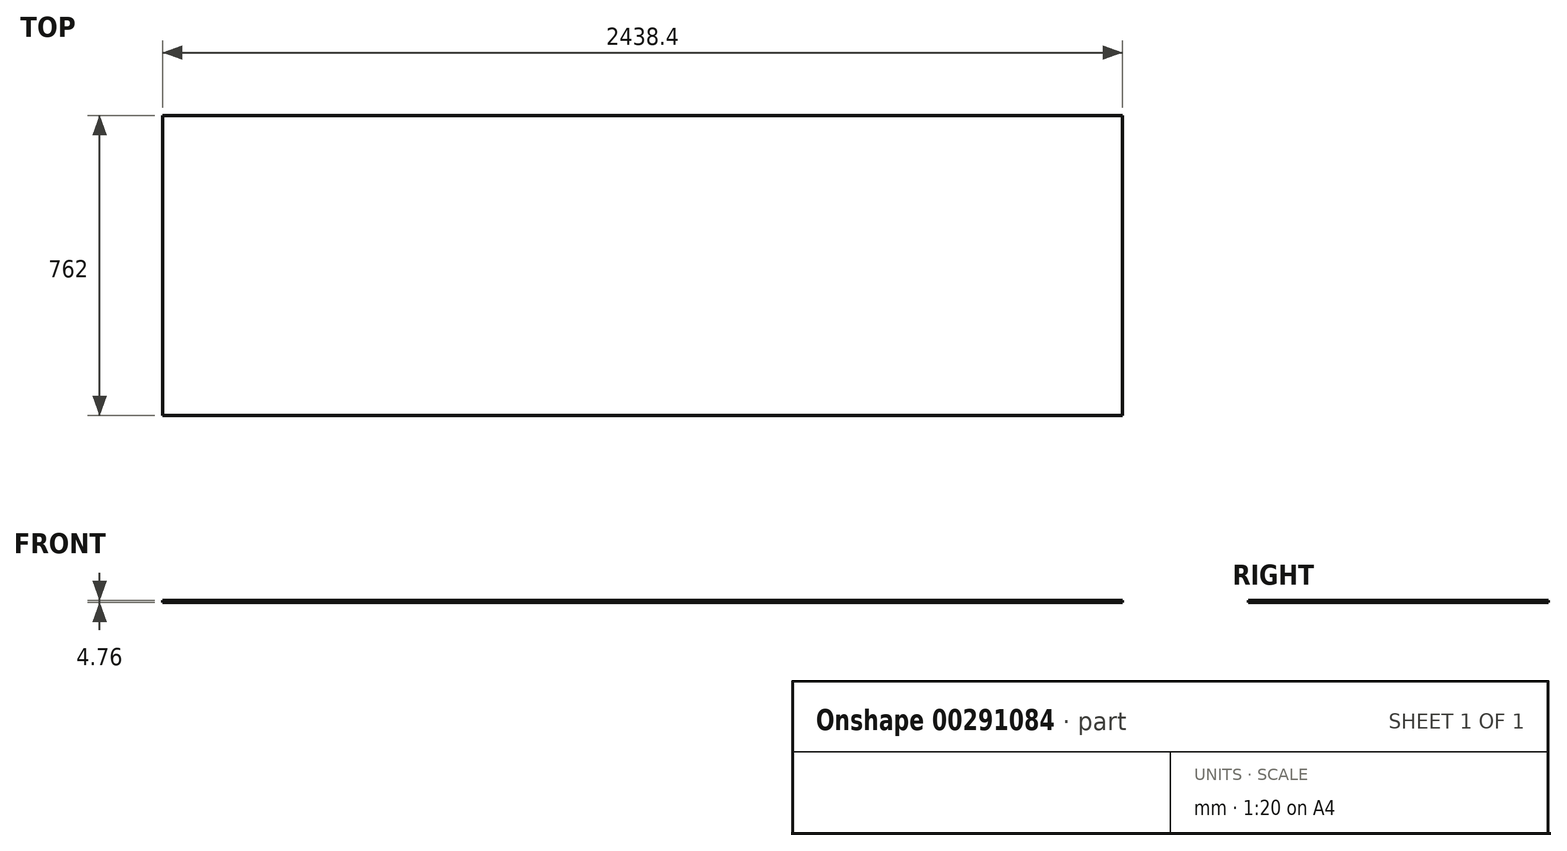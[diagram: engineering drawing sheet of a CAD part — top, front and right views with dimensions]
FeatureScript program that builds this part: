
annotation { "Feature Type Name" : "Feature", "Feature Type Description" : "" }
export const myFeature = defineFeature(function(context is Context, id is Id, definition is map)
    precondition{}
    {
        {
            var Q0;
            Q0=qCreatedBy(makeId("Top.planeOp"),FACE);
            var sketch = newSketch(context, id + "F0", { "sketchPlane" : qUnion([Q0])});
            skLineSegment(sketch, "E0.bottom", {"start": v(0, 0) * mm, "end": v(2438.4, 0) * mm});
            skLineSegment(sketch, "E0.top", {"start": v(0, -762) * mm, "end": v(2438.4, -762) * mm});
            skLineSegment(sketch, "E0.left", {"start": v(0, 0) * mm, "end": v(0, -762) * mm});
            skLineSegment(sketch, "E0.right", {"start": v(2438.4, 0) * mm, "end": v(2438.4, -762) * mm});
            skSolve(sketch);
        }
        {
            var Q0;
            Q0=qSketchRegion(id+"F0",true);
            extrude(context, id + "F1", {"entities" : qUnion([Q0]), "oppositeDirection" : true, "depth" : 4.76 * mm});
        }
    });
